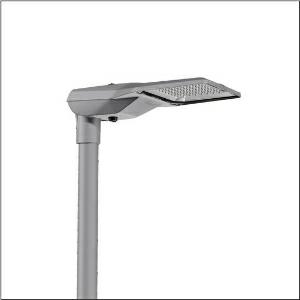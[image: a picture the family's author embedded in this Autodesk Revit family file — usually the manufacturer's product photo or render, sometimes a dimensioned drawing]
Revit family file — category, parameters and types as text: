
# Revit family: streetlight_sl_21_midi___stw1_0a_5xe3e33t08mb_6392
name_source: partatom
category: Lighting Fixtures
units: mm (PartAtom-declared; Revit-internal decimal feet)

## family parameters
Cut with Voids When Loaded = No
Host = Face
Light Source = No
Part Type = Normal
Room Calculation Point = No
Round Connector Dimension = Use Diameter
Shared = No

## types (1)
- --- (1 x LED, 18270 lm, 136 W, 3000K)
    Apparent Load = 136 VA
    CIE Flux Codes = 38 75 98 100 100
    Color Rendering = 70
    Color Temperature = 3000K
    Default Elevation = 1800 mm
    Description = Streetlight SL 21 midi, mast luminaire, primary light control with lens, of PMMA, primary optical cover: cover, of toughened safety glass, transparent, light distribution: STW1.0a, light emission: direct distribution, primary light characteristic: asymmetric, installation type: side-entry, post-top, LED, High Power LED, rated luminous flux: 18.270lm, luminous efficacy: 134lm/W, light colour: 730, colour temperature: 3000K, control gear: D4i, control: overheat protection, constant luminous flux control, time-dependent luminous flux control, flexible luminous flux parameterisation, pre-setting: logarithmic dimming characteristic, mains connection: 230..240V, AC, 50/60Hz, start of lifetime: 136W, end of service life: 142W, reduction: 61W, luminaire housing, of diecast aluminium, powder-coated, SITECO metallic grey (DB 702S), corrosivity category C5 high according to DIN EN ISO 12944, please order mast flange separately, inclination adjustable: 0°, 5°, 10°, 15°, sealing non-destructively replaceable, multi-level sealing system, length: 644mm, width: 335mm, height: 110mm, mast flange for spigot size: 42mm (side-entry): 5XC10008XM4, 60/48mm (side-entry/post-top): 5XC10108XM2, 76/60mm (side-entry/post-top): 5XC10108XM1, mounting height: 4..8m, Smart Interface below and above, protection rating (complete): IP66, insulation class (complete): insulation class II (safety insulation), certification: CE, ENEC, ENEC+, VDE, impact resistance: IK10, permissible operating ambient temperature for outdoor applications: -40..+50°C, standard-compliant lighting for roads and squares, packaging unit: 1 piece

Light Distribution: STW1.0a
    Height = 111 mm
    Lamp = 1 x LED
    Lamp Light Flux = 18270 lm
    Lamp Power = 136 W
    Lamp count = 1
    Length = 644 mm
    Luminous efficacy = 134 lm/W
    Manufacturer = Siteco
    ModVariant = No
    Model = 5XE3E33T08MB
    Number of Poles = 1
    OnlyDefault = Yes
    Power Factor = 1
    Product Name = Streetlight SL 21 midi | STW1.0a
    Product group = mast luminaire | pylon top
    ProductGroupID = 6100
    Protection Class = Protection class II
    Protection Degree = IP 66
    RLX_Detail_Level = 1
    RLX_Emergency_Light_Flux = 0 lm
    RLX_Emergency_Type = 0
    RLX_Emergency_Type_DB = No
    RlxData = <blob elided: 26993 chars, md5=ac39ae73>
    Socket = socket
    Standby Power = 0 W
    System Light Flux = 18270 lm
    System Power = 136 W
    Type Comments = factory setting: luminous flux: 100 % | dim-lin: 254 | 695 mA
    Type Image = l_1004304.jpg
    URL = http://relux.com
    VarID = @adj_185373
    Voltage = 0 V
    Weight = 0.00 kg
    Width = 336 mm

## geometry (parser evidence)
native form markers: Blend x4, Sweep x12
no freeform markers — native parametric forms only
